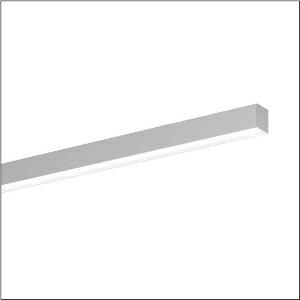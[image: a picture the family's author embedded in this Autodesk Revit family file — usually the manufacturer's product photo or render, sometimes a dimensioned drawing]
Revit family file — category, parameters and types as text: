
# Revit family: silica_r__21_51mx20tbt2s_686e
name_source: partatom
category: Lighting Fixtures
units: mm (PartAtom-declared; Revit-internal decimal feet)

## family parameters
Cut with Voids When Loaded = No
Host = Face
Light Source = No
Part Type = Normal
Room Calculation Point = No
Round Connector Dimension = Use Diameter
Shared = No

## types (1)
- --- (1 x LED, 3000 lm, 25.6 W, 6500K)
    Apparent Load = 26 VA
    CIE Flux Codes = 48 79 96 100 100
    Color Rendering = 80
    Color Temperature = 6500K
    Default Elevation = 1800 mm
    Description = Silica® 21, office luminaire, primary optical cover: cover, of PMMA, opal, light emission: direct distribution, primary light characteristic: symmetric, installation type: surface-mounted, LED, rated luminous flux: 3.000lm, luminous efficacy: 112lm/W, light colour: 8tw, colour temperature: 2700..6500K, control gear: ECG DALI, with terminal, 3+2-pole, max. 2.5mm², mains connection: 220..240V, AC, 50/60Hz, rated input power: 26.9W, luminaire housing, of aluminium, metallic grey (RAL 9006), length: 1.504mm, width: 53mm, height: 53mm, protection rating (complete): IP20, insulation class (complete): insulation class I (protective earthing), certification: CE, permissible operating ambient temperature: 0..+35°C, standard: EN 50419, packaging unit: 1 piece
    Height = 0 mm  [stored 0 ft]
    Lamp = 1 x LED
    Lamp Light Flux = 3000 lm
    Lamp Power = 25.6 W
    Lamp count = 1
    Length = 1504 mm
    Luminous efficacy = 117 lm/W
    Manufacturer = Siteco
    ModVariant = No
    Model = 51MX20TBT2S
    Mounting Place = Ceiling
    Mounting Type = Recessed
    Number of Poles = 1
    OnlyDefault = Yes
    Power Factor = 1
    Product Name = Silica® 21
    Product group = office luminaire | ceiling recessed
    ProductGroupID = 401
    Protection Class = Protection class I
    Protection Degree = IP 20
    RLX_Detail_Level = 1
    RLX_Emergency_Light_Flux = 0 lm
    RLX_Emergency_Type = 0
    RLX_Emergency_Type_DB = No
    RlxData = <blob elided: 23241 chars, md5=3358e682>
    Socket = socket
    Standby Power = 0 W
    System Light Flux = 3000 lm
    System Power = 26 W
    Type Comments = individual setting
    Type Image = l_1297768.jpg
    URL = http://relux.com
    VarID = @adj_070993
    Voltage = 0 V
    Weight = 0.00 kg
    Width = 53 mm

note: [stored X ft] marks values corroborated as IEEE doubles in the binary element streams (Revit-internal decimal feet)

## geometry (parser evidence)
native form markers: Blend x4, Sweep x9
no freeform markers — native parametric forms only
